# Revit family: QF_Scotsman_ECS226WS_ECM226WS_ECL226WS_cat
name_source: partatom
category: Specialty Equipment
revit_build: Autodesk Revit MEP 2012 (Build: 20110916_2132(x64)
units: mm (PartAtom-declared; Revit-internal decimal feet)

## types (3) — shared parameters
Apparent Power = 0 VA
Assembly Code = E1090320
BTUH = 2650 W
Cold Water Connection Height = 512 mm  [stored 1.67979 ft]
Cold Water Maximum Pressure = 5.0 bar
Cold Water Minimum Pressure = 1.0 bar
Cold Water Size = 1"
Conn Conduit = Yes
Cycle = 50 Hz
Depth = 715 mm
Elec Conn Connection Height = 601 mm
FL Amps = 0 A
Height = 1083 mm
Indirect Waste Connection Height = 138 mm
Indirect Waste Size = 1"
Manufacturer = SCOTSMAN
Max Overcurrent Protection = 16 A
Min Ckt Ampacity = 0 A
Phase = 1
Refrigerant Type = R-404a
URL = www.scotsman-ice.com
Volts = 230 V
Watts = 800 W
Weight = 98 kg
Width = 1078 mm  [stored 3.53675 ft]

## per-type parameters (varying)
| type | Description | Model |
| ECS226WS | SELF CONTAINED ICE MACHINE WATER COOLED - SMALL GOURMET 8 g | ECS 226 WS |
| ECM226WS | SELF CONTAINED ICE MACHINE WATER COOLED - MEDIUM GOURMET 20 g | ECM 226 WS |
| ECL226WS | SELF CONTAINED ICE MACHINE WATER COOLED - LARGE GOURMET 39 g | ECL 226 WS |

note: [stored X ft] marks values corroborated as IEEE doubles in the binary element streams (Revit-internal decimal feet)

## geometry (parser evidence)
native form markers: Blend x6, Sweep x1
no freeform markers — native parametric forms only
